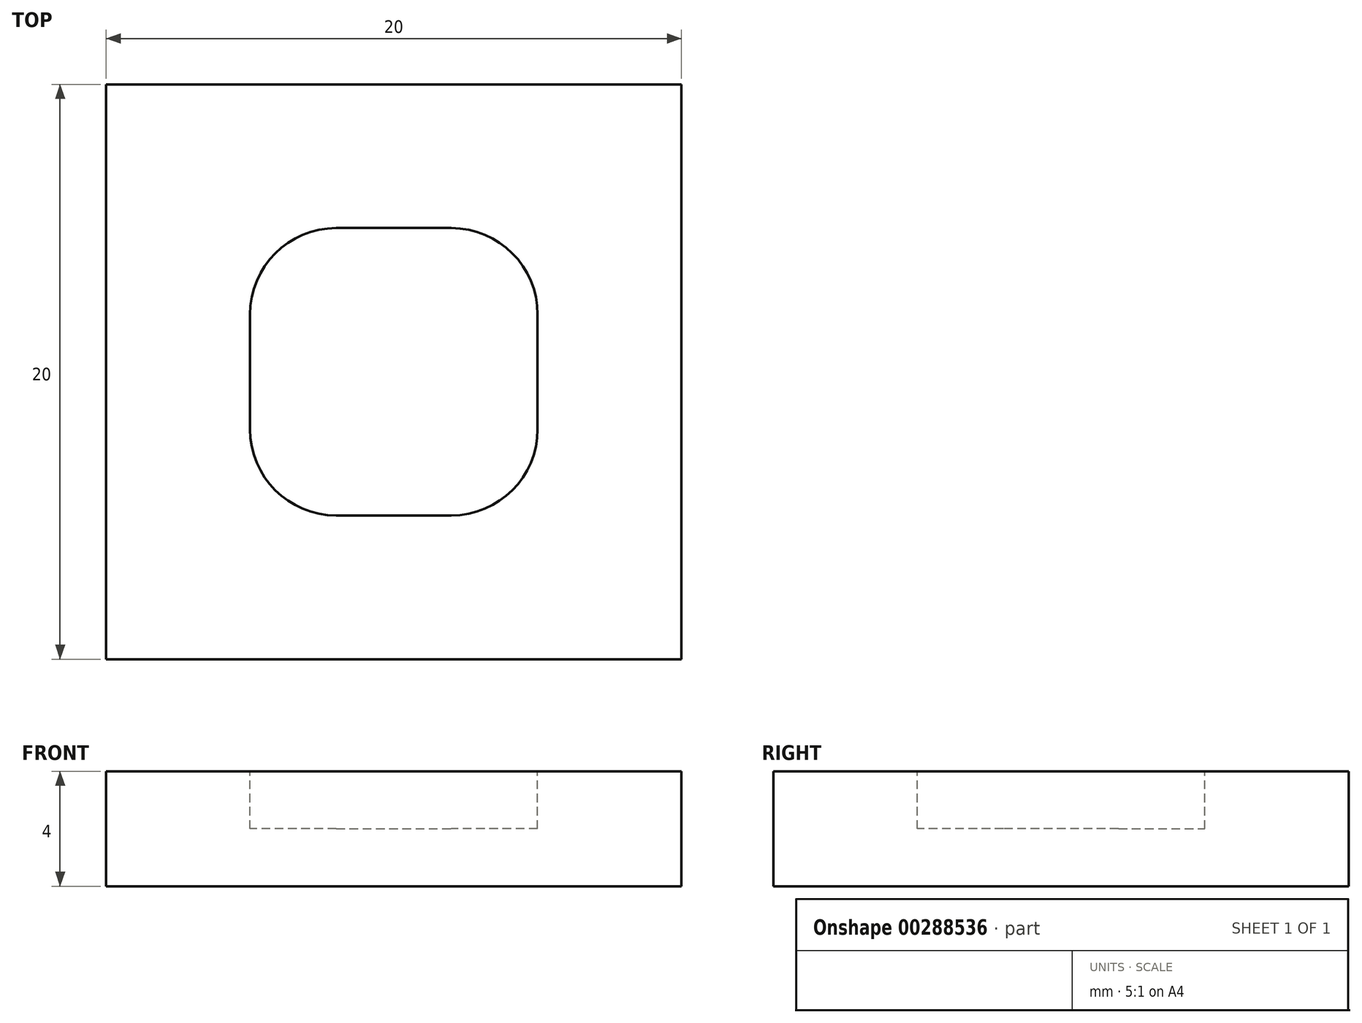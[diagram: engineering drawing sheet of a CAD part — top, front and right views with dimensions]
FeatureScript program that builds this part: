
annotation { "Feature Type Name" : "Feature", "Feature Type Description" : "" }
export const myFeature = defineFeature(function(context is Context, id is Id, definition is map)
    precondition{}
    {
        {
            var Q0;
            Q0=qCreatedBy(makeId("Top.planeOp"),FACE);
            var sketch = newSketch(context, id + "F0", { "sketchPlane" : qUnion([Q0])});
            skLineSegment(sketch, "E0.bottom", {"start": v(10, -10) * mm, "end": v(-10, -10) * mm});
            skLineSegment(sketch, "E0.top", {"start": v(10, 10) * mm, "end": v(-10, 10) * mm});
            skLineSegment(sketch, "E0.left", {"start": v(10, -10) * mm, "end": v(10, 10) * mm});
            skLineSegment(sketch, "E0.right", {"start": v(-10, -10) * mm, "end": v(-10, 10) * mm});
            skPoint(sketch, "E0.middle", {"position": v(0, 0) * mm});
            skLineSegment(sketch, "E1.bottom", {"start": v(-2, 5) * mm, "end": v(2, 5) * mm});
            skLineSegment(sketch, "E1.top", {"start": v(-2, -5) * mm, "end": v(2, -5) * mm});
            skLineSegment(sketch, "E1.left", {"start": v(-5, 2) * mm, "end": v(-5, -2) * mm});
            skLineSegment(sketch, "E1.right", {"start": v(5, 2) * mm, "end": v(5, -2) * mm});
            skPoint(sketch, "E2.visualSharp", {"position": v(-5, 5) * mm});
            skArc(sketch, "E2.filletArc", {"start": v(-2, 5) * mm, "mid": v(-4.12, 4.12) * mm, "end": v(-5, 2) * mm});
            skPoint(sketch, "E3.visualSharp", {"position": v(5, 5) * mm});
            skArc(sketch, "E3.filletArc", {"start": v(5, 2) * mm, "mid": v(4.12, 4.12) * mm, "end": v(2, 5) * mm});
            skPoint(sketch, "E4.visualSharp", {"position": v(5, -5) * mm});
            skArc(sketch, "E4.filletArc", {"start": v(2, -5) * mm, "mid": v(4.12, -4.12) * mm, "end": v(5, -2) * mm});
            skPoint(sketch, "E5.visualSharp", {"position": v(-5, -5) * mm});
            skArc(sketch, "E5.filletArc", {"start": v(-5, -2) * mm, "mid": v(-4.12, -4.12) * mm, "end": v(-2, -5) * mm});
            skSolve(sketch);
        }
        {
            var Q0;
            Q0=makeQuery(id+"F0.imprint","IMPRINT",FACE,{"disambiguationData":[TD([[makeQuery(id+"F0.imprint","IMPRINT",EDGE,{"derivedFrom":sQuery(id+"F0.wireOp",EDGE,"E0.bottom")}),-1.0]])]});
            var Q1;
            Q1=makeQuery(id+"F0.imprint","IMPRINT",FACE,{"disambiguationData":[TD([[makeQuery(id+"F0.imprint","IMPRINT",EDGE,{"derivedFrom":sQuery(id+"F0.wireOp",EDGE,"E1.bottom")}),-1.0]])]});
            extrude(context, id + "F1", {"entities" : qUnion([Q0, Q1]), "oppositeDirection" : true, "depth" : 4 * mm});
        }
        {
            var Q0;
            Q0=makeQuery(id+"F0.imprint","IMPRINT",FACE,{"disambiguationData":[TD([[makeQuery(id+"F0.imprint","IMPRINT",EDGE,{"derivedFrom":sQuery(id+"F0.wireOp",EDGE,"E1.bottom")}),-1.0]])]});
            extrude(context, id + "F2", {"entities" : qUnion([Q0]), "operationType" : NewBodyOperationType.REMOVE, "oppositeDirection" : true, "depth" : 2 * mm});
        }
    });
